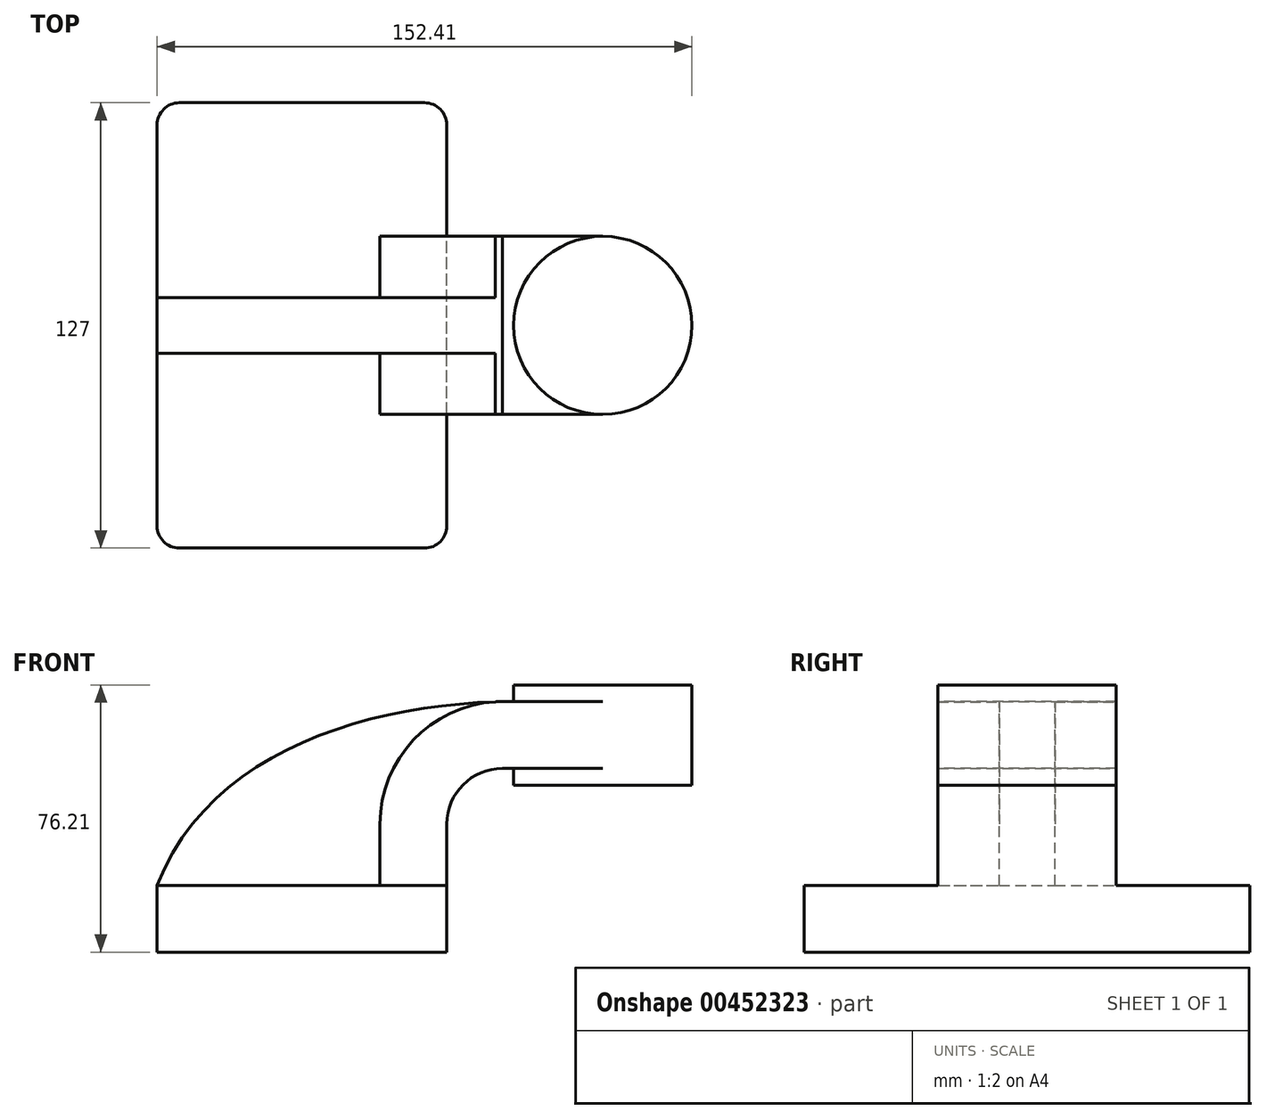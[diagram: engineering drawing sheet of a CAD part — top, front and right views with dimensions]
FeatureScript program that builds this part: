
annotation { "Feature Type Name" : "Feature", "Feature Type Description" : "" }
export const myFeature = defineFeature(function(context is Context, id is Id, definition is map)
    precondition{}
    {
        {
            var Q0;
            Q0=qCreatedBy(makeId("Front.planeOp"),FACE);
            var sketch = newSketch(context, id + "F0", { "sketchPlane" : qUnion([Q0])});
            skLineSegment(sketch, "E0.bottom", {"start": v(41.27, 9.53) * mm, "end": v(-41.28, 9.53) * mm});
            skLineSegment(sketch, "E0.top", {"start": v(41.28, -9.52) * mm, "end": v(-41.27, -9.52) * mm});
            skLineSegment(sketch, "E0.left", {"start": v(41.28, 9.53) * mm, "end": v(41.28, -9.52) * mm});
            skLineSegment(sketch, "E0.right", {"start": v(-41.28, 9.53) * mm, "end": v(-41.27, -9.52) * mm});
            skPoint(sketch, "E0.middle", {"position": v(0, 0) * mm});
            skLineSegment(sketch, "E1.bottom", {"start": v(60.33, 38.1) * mm, "end": v(111.12, 38.1) * mm});
            skLineSegment(sketch, "E1.top", {"start": v(60.33, 66.68) * mm, "end": v(111.12, 66.68) * mm});
            skLineSegment(sketch, "E1.left", {"start": v(60.33, 38.1) * mm, "end": v(60.33, 66.68) * mm});
            skLineSegment(sketch, "E1.right", {"start": v(111.12, 38.1) * mm, "end": v(111.12, 66.68) * mm});
            skPoint(sketch, "E1.middle", {"position": v(85.72, 52.39) * mm});
            skLineSegment(sketch, "E2", {"start": v(41.27, 9.53) * mm, "end": v(41.27, 26.99) * mm});
            skArc(sketch, "E3", {"start": v(41.27, 26.99) * mm, "mid": v(45.92, 38.21) * mm, "end": v(57.15, 42.86) * mm});
            skLineSegment(sketch, "E4", {"start": v(57.15, 42.86) * mm, "end": v(85.73, 42.86) * mm});
            skLineSegment(sketch, "E5.0", {"start": v(57.15, 61.91) * mm, "end": v(85.73, 61.91) * mm});
            skArc(sketch, "E5.1", {"start": v(22.23, 26.99) * mm, "mid": v(32.45, 51.68) * mm, "end": v(57.15, 61.91) * mm});
            skLineSegment(sketch, "E5.2", {"start": v(22.22, 9.53) * mm, "end": v(22.22, 26.99) * mm});
            skLineSegment(sketch, "E6", {"start": v(85.73, 61.91) * mm, "end": v(85.73, 42.86) * mm});
            skFitSpline(sketch, "E7", {"points": [v(-41.28, 9.53) * mm, v(57.15, 61.91) * mm], "startDerivative": vector(44.55, 114.5) * mm, "endDerivative": vector(116.89, 2.81) * mm});
            skLineSegment(sketch, "E8", {"start": v(85.72, 66.68) * mm, "end": v(85.73, 38.1) * mm});
            skSolve(sketch);
        }
        {
            var Q0;
            Q0=makeQuery(id+"F0.imprint","IMPRINT",FACE,{"disambiguationData":[TD([[makeQuery(id+"F0.imprint","IMPRINT",EDGE,{"derivedFrom":sQuery(id+"F0.wireOp",EDGE,"E0.top")}),-1.0]])]});
            extrude(context, id + "F1", {"entities" : qUnion([Q0]), "endBound" : BoundingType.SYMMETRIC, "depth" : 127 * mm});
        }
        {
            var Q0;
            {var subQ1=sQuery(id+"F0.wireOp",EDGE,"E2");Q0=makeQuery(id+"F0.imprint","IMPRINT",FACE,{"disambiguationData":[TD([[makeQuery(id+"F0.imprint","IMPRINT",EDGE,{"derivedFrom":subQ1}),1.0]])]});}
            var Q1;
            {var subQ0=sQuery(id+"F0.wireOp",EDGE,"E4");var subQ1=sQuery(id+"F0.wireOp",EDGE,"E1.left");var subQ2=makeQuery(id+"F0.imprint","INTERSECT",VERTEX,{"derivedFrom":[subQ1,subQ0]});Q1=makeQuery(id+"F0.imprint","IMPRINT",FACE,{"disambiguationData":[TD([[makeQuery(id+"F0.imprint","IMPRINT",EDGE,{"disambiguationData":[TD([[subQ2,-1.0]])],"derivedFrom":subQ1}),-1.0]])]});}
            extrude(context, id + "F2", {"entities" : qUnion([Q0, Q1]), "operationType" : NewBodyOperationType.ADD, "endBound" : BoundingType.SYMMETRIC, "depth" : 50.8 * mm});
        }
        {
            var Q0;
            {var subQ3=sQuery(id+"F0.wireOp",EDGE,"E5.2");Q0=makeQuery(id+"F0.imprint","IMPRINT",FACE,{"disambiguationData":[TD([[makeQuery(id+"F0.imprint","IMPRINT",EDGE,{"derivedFrom":subQ3}),1.0]])]});}
            extrude(context, id + "F3", {"entities" : qUnion([Q0]), "operationType" : NewBodyOperationType.ADD, "endBound" : BoundingType.SYMMETRIC, "depth" : 15.88 * mm});
        }
        {
            var Q0;
            {var subQ4=sQuery(id+"F0.wireOp",EDGE,"E1.right");Q0=makeQuery(id+"F0.imprint","IMPRINT",FACE,{"disambiguationData":[TD([[makeQuery(id+"F0.imprint","IMPRINT",EDGE,{"derivedFrom":subQ4}),1.0]])]});}
            var Q1;
            Q1=sQuery(id+"F0.wireOp",EDGE,"E8");
            revolve(context, id + "F4", {"operationType" : NewBodyOperationType.ADD, "entities" : qUnion([Q0]), "axis" : qUnion([Q1]), "revolveType" : RevolveType.FULL});
        }
        {
            var Q0;
            Q0=makeQuery(id+"F1.opExtrude","CAP_EDGE",EDGE,{"disambiguationData":[OSD([sQuery(id+"F0.wireOp",EDGE,"E0.left")])],"isStart":false});
            var Q1;
            Q1=makeQuery(id+"F1.opExtrude","CAP_EDGE",EDGE,{"disambiguationData":[OSD([sQuery(id+"F0.wireOp",EDGE,"E0.right")])],"isStart":false});
            var Q2;
            Q2=makeQuery(id+"F1.opExtrude","CAP_EDGE",EDGE,{"disambiguationData":[OSD([sQuery(id+"F0.wireOp",EDGE,"E0.left")])],"isStart":true});
            var Q3;
            Q3=makeQuery(id+"F1.opExtrude","CAP_EDGE",EDGE,{"disambiguationData":[OSD([sQuery(id+"F0.wireOp",EDGE,"E0.right")])],"isStart":true});
            fillet(context, id + "F5", {"entities" : qUnion([Q0, Q1, Q2, Q3]), "radius" : 6.35 * mm, "tangentPropagation" : true, "allowEdgeOverflow" : false});
        }
    });
